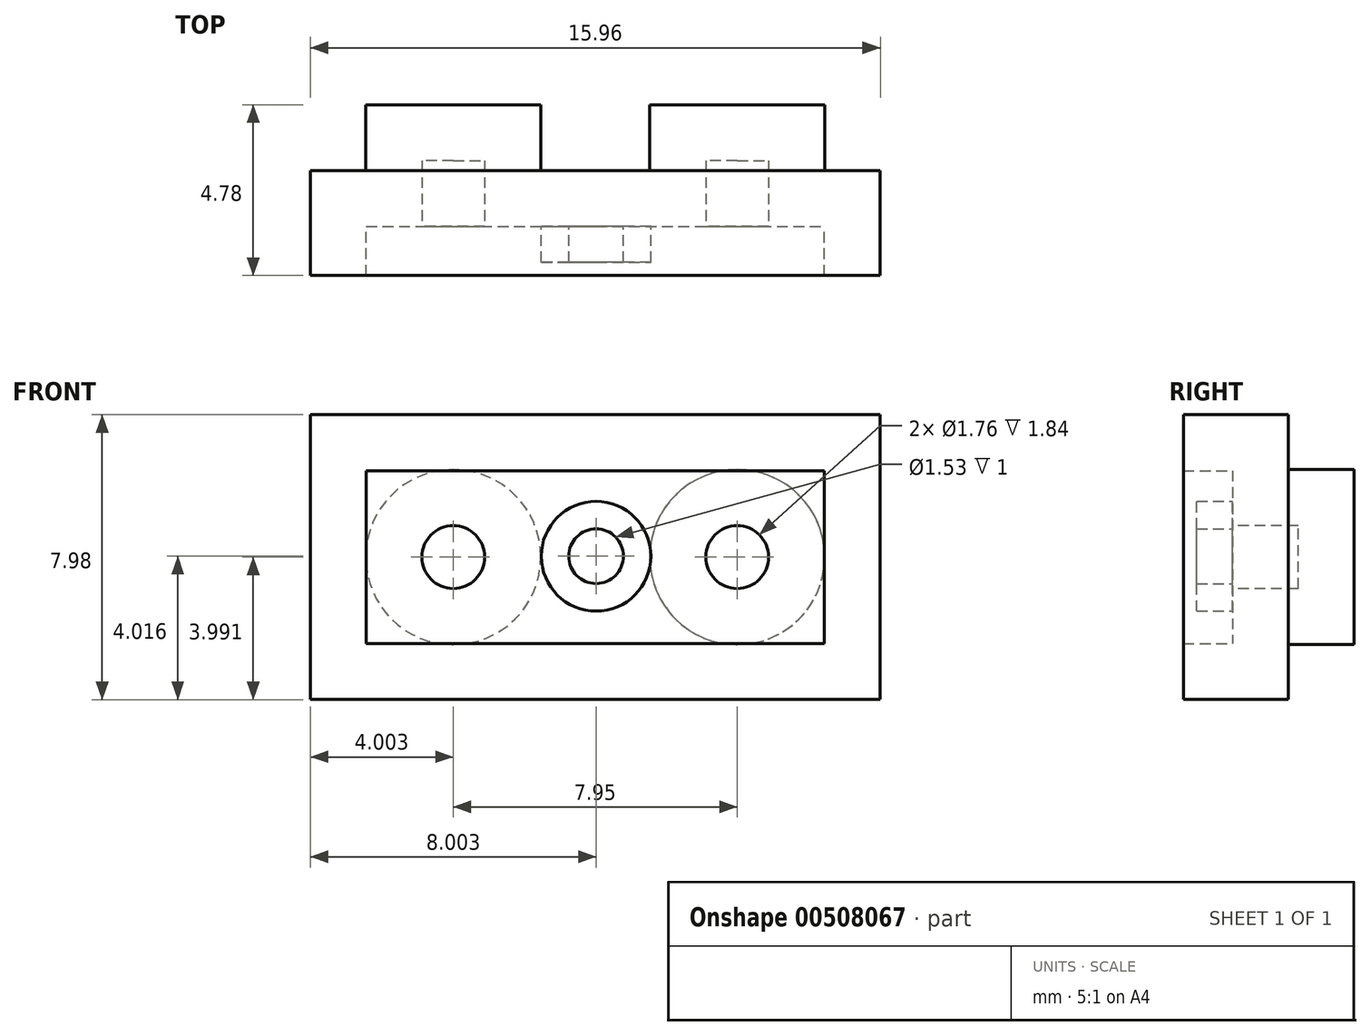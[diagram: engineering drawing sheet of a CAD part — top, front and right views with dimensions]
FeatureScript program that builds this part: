
annotation { "Feature Type Name" : "Feature", "Feature Type Description" : "" }
export const myFeature = defineFeature(function(context is Context, id is Id, definition is map)
    precondition{}
    {
        {
            var Q0;
            Q0=qCreatedBy(makeId("Front.planeOp"),FACE);
            var sketch = newSketch(context, id + "F0", { "sketchPlane" : qUnion([Q0])});
            skLineSegment(sketch, "E0.bottom", {"start": v(-7.84, 9.03) * mm, "end": v(8.12, 9.03) * mm});
            skLineSegment(sketch, "E0.top", {"start": v(-7.84, 1.05) * mm, "end": v(8.12, 1.05) * mm});
            skLineSegment(sketch, "E0.left", {"start": v(-7.84, 9.03) * mm, "end": v(-7.84, 1.05) * mm});
            skLineSegment(sketch, "E0.right", {"start": v(8.12, 9.03) * mm, "end": v(8.12, 1.05) * mm});
            skSolve(sketch);
        }
        {
            var Q0;
            Q0 = qSketchRegion(id + "F0", true);
            extrude(context, id + "F1", {"entities" : qUnion([Q0]), "depth" : 2.94 * mm, "offsetDistance" : 25 * mm});
        }
        {
            var Q0;
            Q0=makeQuery(id+"F1.opExtrude","CAP_FACE",FACE,{"disambiguationData":[OSD([sQuery(id+"F0.wireOp",EDGE,"E0.bottom"),sQuery(id+"F0.wireOp",EDGE,"E0.top"),sQuery(id+"F0.wireOp",EDGE,"E0.left"),sQuery(id+"F0.wireOp",EDGE,"E0.right")])],"isStart":true});
            var sketch = newSketch(context, id + "F2", { "sketchPlane" : qUnion([Q0])});
            skCircle(sketch, "E1", {"center": v(3.84, 5.04) * mm, "radius": 2.45 * mm});
            skCircle(sketch, "E2", {"center": v(-4.11, 5.04) * mm, "radius": 2.45 * mm});
            skSolve(sketch);
        }
        {
            var Q0;
            Q0 = qSketchRegion(id + "F2", true);
            extrude(context, id + "F3", {"entities" : qUnion([Q0]), "operationType" : NewBodyOperationType.ADD, "depth" : 1.84 * mm, "offsetDistance" : 25 * mm});
        }
        {
            var Q0;
            Q0=makeQuery(id+"F1.opExtrude","CAP_FACE",FACE,{"disambiguationData":[OSD([sQuery(id+"F0.wireOp",EDGE,"E0.bottom"),sQuery(id+"F0.wireOp",EDGE,"E0.top"),sQuery(id+"F0.wireOp",EDGE,"E0.left"),sQuery(id+"F0.wireOp",EDGE,"E0.right")])],"isStart":false});
            shell(context, id + "F4", {"entities" : qUnion([Q0]), "thickness" : 1.57 * mm});
        }
        {
            var Q0;
            Q0=makeQuery(id+"F4.opShell","OFFSET_FACE",FACE,{"disambiguationData":[OSD([sQuery(id+"F0.wireOp",EDGE,"E0.bottom"),sQuery(id+"F0.wireOp",EDGE,"E0.top"),sQuery(id+"F0.wireOp",EDGE,"E0.left"),sQuery(id+"F0.wireOp",EDGE,"E0.right")])]});
            var sketch = newSketch(context, id + "F5", { "sketchPlane" : qUnion([Q0])});
            skCircle(sketch, "E3", {"center": v(0.16, 5.07) * mm, "radius": 1.53 * mm});
            skCircle(sketch, "E4", {"center": v(0.16, 5.07) * mm, "radius": 0.77 * mm});
            skSolve(sketch);
        }
        {
            var Q0;
            Q0 = qSketchRegion(id + "F5", true);
            extrude(context, id + "F6", {"entities" : qUnion([Q0]), "operationType" : NewBodyOperationType.ADD, "depth" : 1 * mm, "offsetDistance" : 25 * mm});
        }
    });
